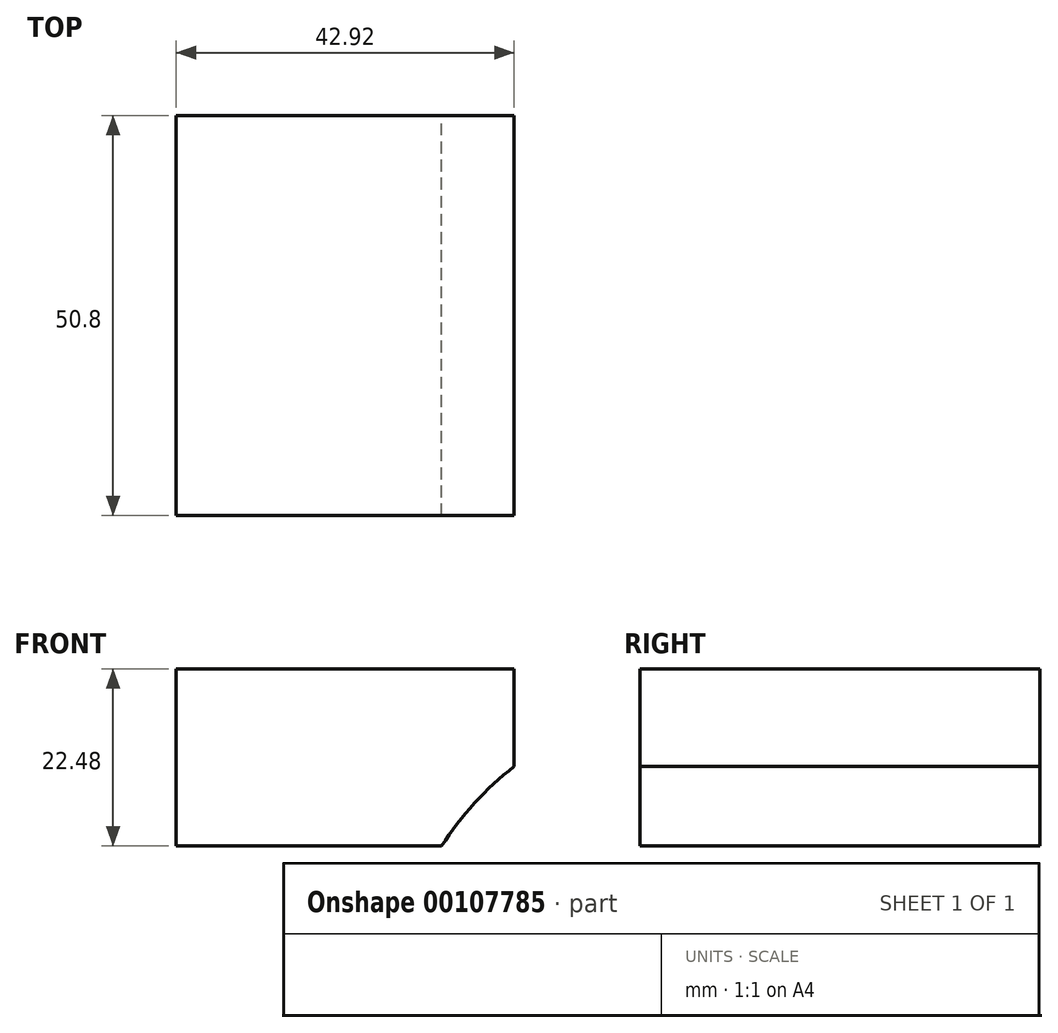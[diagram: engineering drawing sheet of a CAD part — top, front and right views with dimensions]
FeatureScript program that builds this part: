
annotation { "Feature Type Name" : "Feature", "Feature Type Description" : "" }
export const myFeature = defineFeature(function(context is Context, id is Id, definition is map)
    precondition{}
    {
        {
            var Q0;
            Q0=qCreatedBy(makeId("Front.planeOp"),FACE);
            var sketch = newSketch(context, id + "F0", { "sketchPlane" : qUnion([Q0])});
            skLineSegment(sketch, "E0.bottom", {"start": v(-68.03, 44.52) * mm, "end": v(-25.1, 44.52) * mm});
            skLineSegment(sketch, "E0.top", {"start": v(-68.03, 22.04) * mm, "end": v(-25.1, 22.04) * mm});
            skLineSegment(sketch, "E0.left", {"start": v(-68.03, 44.52) * mm, "end": v(-68.03, 22.04) * mm});
            skLineSegment(sketch, "E0.right", {"start": v(-25.1, 44.52) * mm, "end": v(-25.1, 22.04) * mm});
            skCircle(sketch, "E1", {"center": v(0, 0) * mm, "radius": 40.78 * mm});
            skSolve(sketch);
        }
        {
            var Q0;
            {var subQ1=sQuery(id+"F0.wireOp",EDGE,"E0.bottom");Q0=makeQuery(id+"F0.imprint","IMPRINT",FACE,{"disambiguationData":[TD([[makeQuery(id+"F0.imprint","IMPRINT",EDGE,{"derivedFrom":subQ1}),-1.0]])]});}
            extrude(context, id + "F1", {"entities" : qUnion([Q0]), "depth" : 25.4 * mm});
        }
        {
            var Q0;
            Q0=makeQuery(id+"F1.opExtrude","CAP_FACE",FACE,{"disambiguationData":[OSD([sQuery(id+"F0.wireOp",EDGE,"E0.bottom"),sQuery(id+"F0.wireOp",EDGE,"E0.top"),sQuery(id+"F0.wireOp",EDGE,"E0.left"),sQuery(id+"F0.wireOp",EDGE,"E0.right"),sQuery(id+"F0.wireOp",EDGE,"E1")])],"isStart":true});
            var sketch = newSketch(context, id + "F2", { "sketchPlane" : qUnion([Q0])});
            skSolve(sketch);
        }
        {
            var Q0;
            Q0=makeQuery(id+"F2.imprint","IMPRINT",FACE,{"disambiguationData":[TD([[makeQuery(id+"F2.imprint","IMPRINT",EDGE,{"derivedFrom":makeQuery(id+"F1.opExtrude","CAP_EDGE",EDGE,{"disambiguationData":[OSD([sQuery(id+"F0.wireOp",EDGE,"E0.bottom")])],"isStart":true})}),1.0]])]});
            extrude(context, id + "F3", {"entities" : qUnion([Q0]), "operationType" : NewBodyOperationType.ADD, "depth" : 25.4 * mm});
        }
    });
